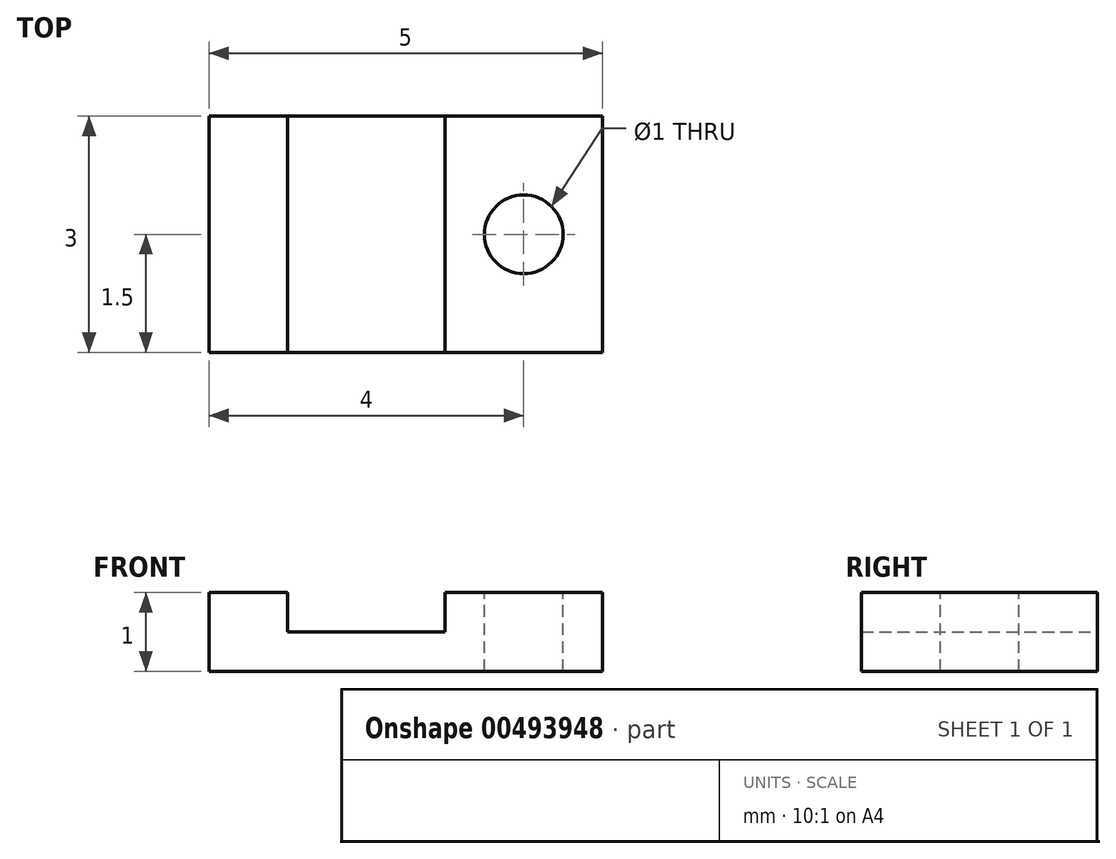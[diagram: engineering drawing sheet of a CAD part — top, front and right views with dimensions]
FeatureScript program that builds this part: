
annotation { "Feature Type Name" : "Feature", "Feature Type Description" : "" }
export const myFeature = defineFeature(function(context is Context, id is Id, definition is map)
    precondition{}
    {
        {
            var Q0;
            Q0=qCreatedBy(makeId("Front.planeOp"),FACE);
            var sketch = newSketch(context, id + "F0", { "sketchPlane" : qUnion([Q0])});
            skLineSegment(sketch, "E0", {"start": v(-1.5, 0) * mm, "end": v(-1.5, 1) * mm});
            skLineSegment(sketch, "E1", {"start": v(-1.5, 1) * mm, "end": v(-0.5, 1) * mm});
            skLineSegment(sketch, "E2", {"start": v(-0.5, 1) * mm, "end": v(-0.5, 0.5) * mm});
            skLineSegment(sketch, "E3", {"start": v(-0.5, 0.5) * mm, "end": v(1.5, 0.5) * mm});
            skLineSegment(sketch, "E4", {"start": v(1.5, 0.5) * mm, "end": v(1.5, 1) * mm});
            skLineSegment(sketch, "E5", {"start": v(1.5, 1) * mm, "end": v(3.5, 1) * mm});
            skLineSegment(sketch, "E6", {"start": v(3.5, 1) * mm, "end": v(3.5, 0) * mm});
            skLineSegment(sketch, "E7", {"start": v(3.5, 0) * mm, "end": v(-1.5, 0) * mm});
            skSolve(sketch);
        }
        {
            var Q0;
            Q0=makeQuery(id+"F0.imprint","IMPRINT",FACE,{"disambiguationData":[TD([[makeQuery(id+"F0.imprint","IMPRINT",EDGE,{"derivedFrom":sQuery(id+"F0.wireOp",EDGE,"E0")}),-1.0]])]});
            extrude(context, id + "F1", {"entities" : qUnion([Q0]), "depth" : 3 * mm});
        }
        {
            var Q0;
            Q0=makeQuery(id+"F1.opExtrude","SWEPT_FACE",FACE,{"disambiguationData":[OSD([sQuery(id+"F0.wireOp",EDGE,"E5")])]});
            var sketch = newSketch(context, id + "F2", { "sketchPlane" : qUnion([Q0])});
            skCircle(sketch, "E8", {"center": v(2.5, -1.5) * mm, "radius": 0.5 * mm});
            skSolve(sketch);
        }
        {
            var Q0;
            Q0=makeQuery(id+"F2.imprint","IMPRINT",FACE,{"disambiguationData":[TD([[makeQuery(id+"F2.imprint","IMPRINT",EDGE,{"derivedFrom":sQuery(id+"F2.wireOp",EDGE,"E8")}),1.0]])]});
            extrude(context, id + "F3", {"entities" : qUnion([Q0]), "operationType" : NewBodyOperationType.REMOVE, "oppositeDirection" : true, "depth" : 25 * mm});
        }
    });
